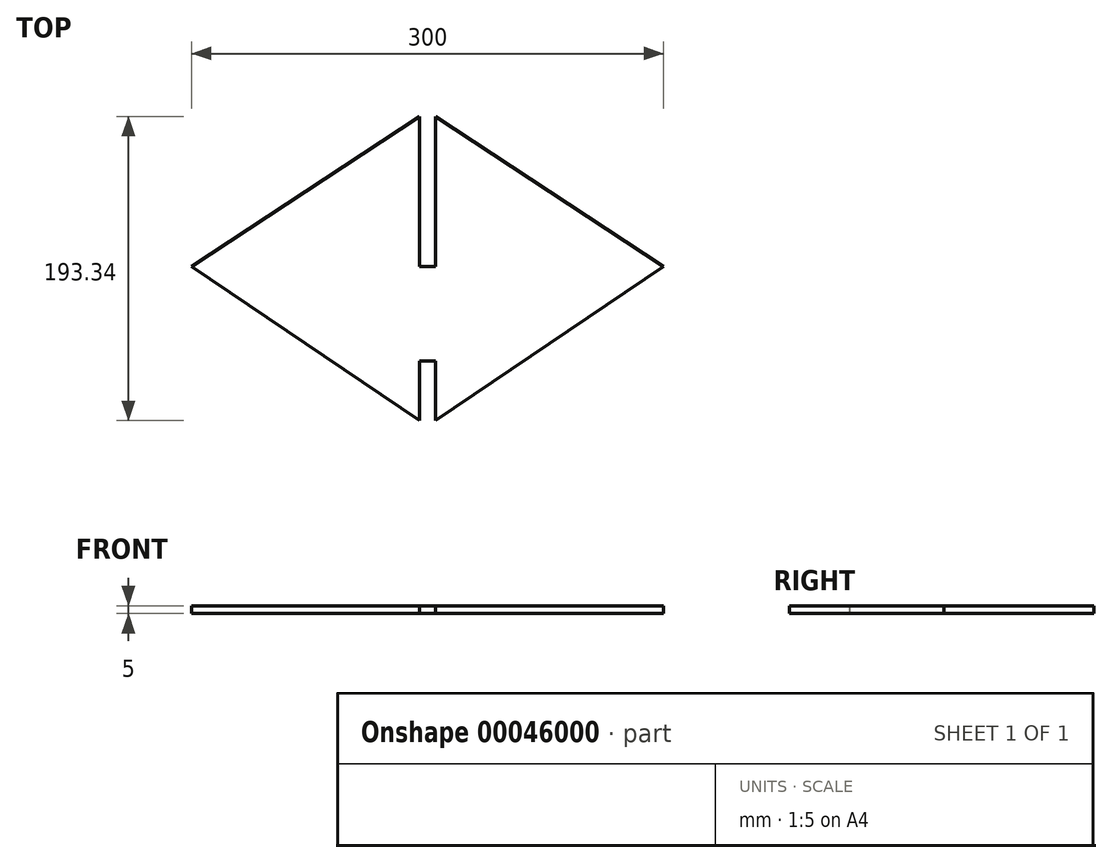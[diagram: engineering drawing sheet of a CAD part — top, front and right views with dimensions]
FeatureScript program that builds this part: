
annotation { "Feature Type Name" : "Feature", "Feature Type Description" : "" }
export const myFeature = defineFeature(function(context is Context, id is Id, definition is map)
    precondition{}
    {
        {
            var Q0;
            Q0=qCreatedBy(makeId("Top.planeOp"),FACE);
            var sketch = newSketch(context, id + "F0", { "sketchPlane" : qUnion([Q0])});
            skLineSegment(sketch, "E0", {"start": v(-152.06, 0) * mm, "end": v(152.06, 0) * mm, "construction": true});
            skPoint(sketch, "E1", {"position": v(0, 128.57) * mm});
            skPoint(sketch, "E2", {"position": v(-150, 30) * mm});
            skPoint(sketch, "E3", {"position": v(150, 30) * mm});
            skLineSegment(sketch, "E4", {"start": v(150, 30) * mm, "end": v(0, 128.57) * mm, "construction": true});
            skLineSegment(sketch, "E5", {"start": v(-150, 30) * mm, "end": v(0, 128.57) * mm, "construction": true});
            skLineSegment(sketch, "E6", {"start": v(0, 143.75) * mm, "end": v(0, -143.75) * mm, "construction": true});
            skLineSegment(sketch, "E7", {"start": v(-150, 30) * mm, "end": v(150, 30) * mm, "construction": true});
            skLineSegment(sketch, "E8", {"start": v(-5, -30) * mm, "end": v(5, -30) * mm});
            skLineSegment(sketch, "E9", {"start": v(5, -30) * mm, "end": v(5, -68.05) * mm});
            skLineSegment(sketch, "E10", {"start": v(-5, -30) * mm, "end": v(-5, -68.05) * mm});
            skLineSegment(sketch, "E11", {"start": v(-5, -68.05) * mm, "end": v(-150, 30) * mm});
            skLineSegment(sketch, "E12", {"start": v(5, -68.05) * mm, "end": v(150, 30) * mm});
            skLineSegment(sketch, "E13", {"start": v(-5, 30) * mm, "end": v(-5, 125.29) * mm});
            skLineSegment(sketch, "E14", {"start": v(5, 30) * mm, "end": v(5, 125.29) * mm});
            skLineSegment(sketch, "E15", {"start": v(-150, 30) * mm, "end": v(-5, 125.29) * mm});
            skLineSegment(sketch, "E16", {"start": v(5, 125.29) * mm, "end": v(150, 30) * mm});
            skLineSegment(sketch, "E17", {"start": v(-5, 30) * mm, "end": v(5, 30) * mm});
            skLineSegment(sketch, "E18", {"start": v(-150, 30) * mm, "end": v(0, -71.43) * mm, "construction": true});
            skLineSegment(sketch, "E19", {"start": v(0, -71.43) * mm, "end": v(150, 30) * mm, "construction": true});
            skSolve(sketch);
        }
        {
            var Q0;
            Q0=makeQuery(id+"F0.imprint","IMPRINT",FACE,{"disambiguationData":[TD([[makeQuery(id+"F0.imprint","IMPRINT",EDGE,{"derivedFrom":sQuery(id+"F0.wireOp",EDGE,"E8")}),1.0]])]});
            extrude(context, id + "F1", {"entities" : qUnion([Q0]), "depth" : 5 * mm});
        }
    });
